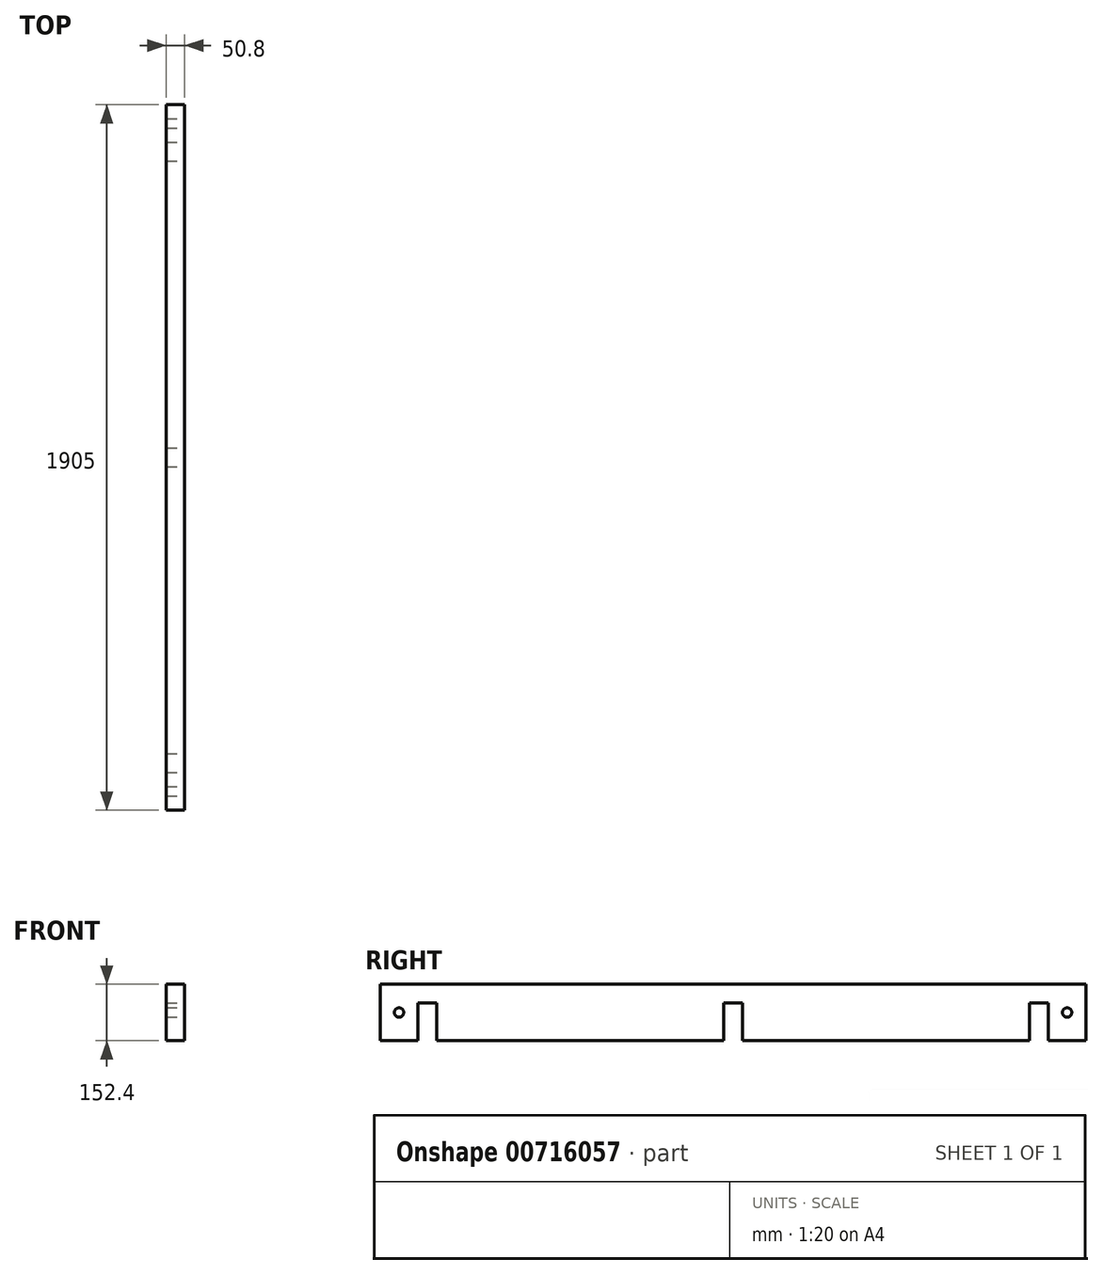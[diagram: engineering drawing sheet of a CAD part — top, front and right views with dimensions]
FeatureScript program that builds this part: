
annotation { "Feature Type Name" : "Feature", "Feature Type Description" : "" }
export const myFeature = defineFeature(function(context is Context, id is Id, definition is map)
    precondition{}
    {
        {
            var Q0;
            Q0=qCreatedBy(makeId("Right.planeOp"),FACE);
            var sketch = newSketch(context, id + "F0", { "sketchPlane" : qUnion([Q0])});
            skLineSegment(sketch, "E0.bottom", {"start": v(1905, 152.4) * mm, "end": v(0, 152.4) * mm});
            skLineSegment(sketch, "E0.top", {"start": v(1905, 0) * mm, "end": v(0, 0) * mm});
            skLineSegment(sketch, "E0.left", {"start": v(1905, 152.4) * mm, "end": v(1905, 0) * mm});
            skLineSegment(sketch, "E0.right", {"start": v(0, 152.4) * mm, "end": v(0, 0) * mm});
            skSolve(sketch);
        }
        {
            var Q0;
            Q0=makeQuery(id+"F0.imprint","IMPRINT",FACE,{"disambiguationData":[TD([[makeQuery(id+"F0.imprint","IMPRINT",EDGE,{"derivedFrom":sQuery(id+"F0.wireOp",EDGE,"E0.bottom")}),1.0]])]});
            extrude(context, id + "F1", {"entities" : qUnion([Q0]), "depth" : 50.8 * mm, "offsetDistance" : 25.4 * mm});
        }
        {
            var Q0;
            Q0=makeQuery(id+"F1.opExtrude","CAP_FACE",FACE,{"disambiguationData":[OSD([sQuery(id+"F0.wireOp",EDGE,"E0.bottom"),sQuery(id+"F0.wireOp",EDGE,"E0.top"),sQuery(id+"F0.wireOp",EDGE,"E0.left"),sQuery(id+"F0.wireOp",EDGE,"E0.right")])],"isStart":false});
            var sketch = newSketch(context, id + "F2", { "sketchPlane" : qUnion([Q0])});
            skLineSegment(sketch, "E1.bottom", {"start": v(101.6, 101.6) * mm, "end": v(152.4, 101.6) * mm});
            skLineSegment(sketch, "E1.top", {"start": v(101.6, 0) * mm, "end": v(152.4, 0) * mm});
            skLineSegment(sketch, "E1.left", {"start": v(101.6, 101.6) * mm, "end": v(101.6, 0) * mm});
            skLineSegment(sketch, "E1.right", {"start": v(152.4, 101.6) * mm, "end": v(152.4, 0) * mm});
            skLineSegment(sketch, "E2", {"start": v(0, 101.6) * mm, "end": v(101.6, 101.6) * mm, "construction": true});
            skLineSegment(sketch, "E3.bottom", {"start": v(1752.6, 101.6) * mm, "end": v(1803.4, 101.6) * mm});
            skLineSegment(sketch, "E3.top", {"start": v(1752.6, 0) * mm, "end": v(1803.4, 0) * mm});
            skLineSegment(sketch, "E3.left", {"start": v(1752.6, 101.6) * mm, "end": v(1752.6, 0) * mm});
            skLineSegment(sketch, "E3.right", {"start": v(1803.4, 101.6) * mm, "end": v(1803.4, 0) * mm});
            skLineSegment(sketch, "E4", {"start": v(0, 0) * mm, "end": v(50.8, 0) * mm});
            skLineSegment(sketch, "E5", {"start": v(50.8, 0) * mm, "end": v(101.6, 0) * mm});
            skLineSegment(sketch, "E6", {"start": v(50.8, 25.4) * mm, "end": v(50.8, 0) * mm, "construction": true});
            skLineSegment(sketch, "E7", {"start": v(1803.4, 0) * mm, "end": v(1905, 0) * mm, "construction": true});
            skLineSegment(sketch, "E8", {"start": v(1905, 101.6) * mm, "end": v(1854.2, 101.6) * mm, "construction": true});
            skLineSegment(sketch, "E9", {"start": v(1854.2, 101.6) * mm, "end": v(1803.4, 101.6) * mm, "construction": true});
            skLineSegment(sketch, "E10", {"start": v(1854.2, 101.6) * mm, "end": v(1854.2, 76.2) * mm, "construction": true});
            skLineSegment(sketch, "E11", {"start": v(50.8, 76.2) * mm, "end": v(50.8, 101.6) * mm, "construction": true});
            skLineSegment(sketch, "E12", {"start": v(1854.2, 25.4) * mm, "end": v(1854.2, 0) * mm, "construction": true});
            skCircle(sketch, "E13", {"center": v(50.8, 76.2) * mm, "radius": 12.7 * mm});
            skCircle(sketch, "E14", {"center": v(1854.2, 76.2) * mm, "radius": 12.7 * mm});
            skLineSegment(sketch, "E15", {"start": v(1854.2, 25.4) * mm, "end": v(1854.2, 50.8) * mm, "construction": true});
            skLineSegment(sketch, "E16", {"start": v(1854.2, 50.8) * mm, "end": v(1854.2, 76.2) * mm, "construction": true});
            skLineSegment(sketch, "E17", {"start": v(50.8, 25.4) * mm, "end": v(50.8, 50.8) * mm, "construction": true});
            skLineSegment(sketch, "E18", {"start": v(50.8, 50.8) * mm, "end": v(50.8, 76.2) * mm, "construction": true});
            skLineSegment(sketch, "E19.bottom", {"start": v(927.1, 101.6) * mm, "end": v(977.9, 101.6) * mm});
            skLineSegment(sketch, "E19.top", {"start": v(927.1, 0) * mm, "end": v(977.9, 0) * mm});
            skLineSegment(sketch, "E19.left", {"start": v(927.1, 101.6) * mm, "end": v(927.1, 0) * mm});
            skLineSegment(sketch, "E19.right", {"start": v(977.9, 101.6) * mm, "end": v(977.9, 0) * mm});
            skSolve(sketch);
        }
        {
            var Q0;
            Q0 = qSketchRegion(id + "F2", true);
            extrude(context, id + "F3", {"entities" : qUnion([Q0]), "operationType" : NewBodyOperationType.REMOVE, "endBound" : BoundingType.THROUGH_ALL, "oppositeDirection" : true, "depth" : 25.4 * mm, "offsetDistance" : 25.4 * mm});
        }
    });
